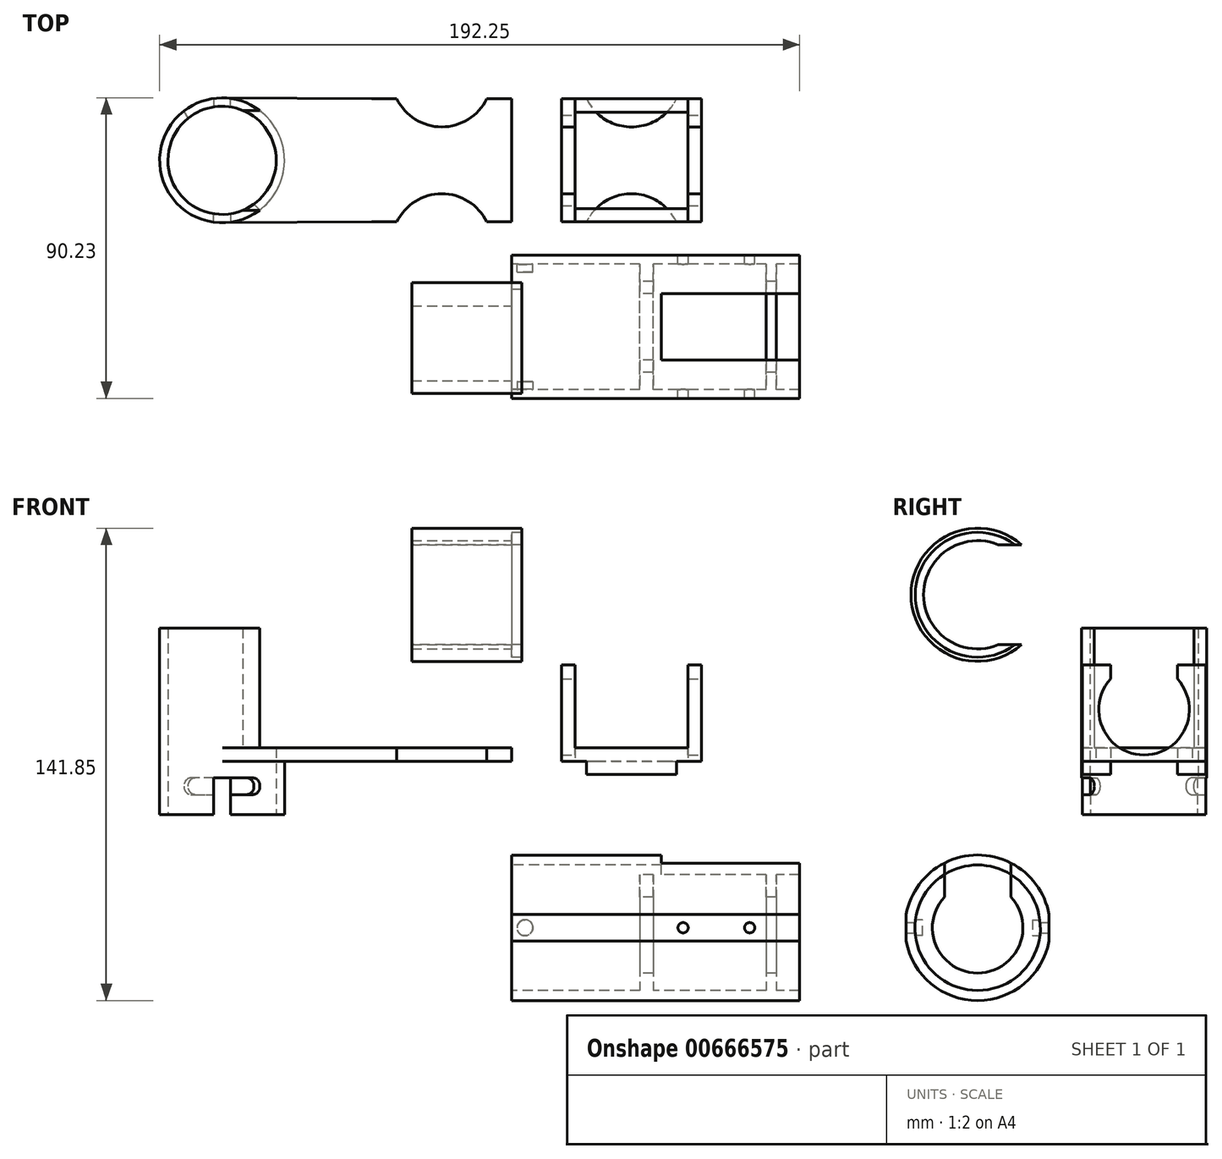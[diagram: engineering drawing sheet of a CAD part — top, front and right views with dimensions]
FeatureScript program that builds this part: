
annotation { "Feature Type Name" : "Feature", "Feature Type Description" : "" }
export const myFeature = defineFeature(function(context is Context, id is Id, definition is map)
    precondition{}
    {
        {
            var Q0;
            Q0=qCreatedBy(makeId("Top.planeOp"),FACE);
            var sketch = newSketch(context, id + "F0", { "sketchPlane" : qUnion([Q0])});
            skLineSegment(sketch, "E0.bottom", {"start": v(0, 18.5) * mm, "end": v(-42, 18.5) * mm});
            skLineSegment(sketch, "E0.top", {"start": v(0, -18.5) * mm, "end": v(-42, -18.5) * mm});
            skLineSegment(sketch, "E0.left", {"start": v(0, 18.5) * mm, "end": v(0, -18.5) * mm});
            skLineSegment(sketch, "E0.right", {"start": v(-42, 18.5) * mm, "end": v(-42, -18.5) * mm});
            skLineSegment(sketch, "E1.bottom", {"start": v(15, 18.5) * mm, "end": v(57, 18.5) * mm});
            skLineSegment(sketch, "E1.top", {"start": v(15, -18.5) * mm, "end": v(57, -18.5) * mm});
            skLineSegment(sketch, "E1.left", {"start": v(15, 18.5) * mm, "end": v(15, -18.5) * mm});
            skLineSegment(sketch, "E1.right", {"start": v(57, 18.5) * mm, "end": v(57, -18.5) * mm});
            skLineSegment(sketch, "E2", {"start": v(19, 18.5) * mm, "end": v(19, -18.5) * mm});
            skLineSegment(sketch, "E3", {"start": v(53, 18.5) * mm, "end": v(53, -18.5) * mm});
            skLineSegment(sketch, "E4", {"start": v(57, -14.5) * mm, "end": v(15, -14.5) * mm});
            skLineSegment(sketch, "E5", {"start": v(15, 14.5) * mm, "end": v(57, 14.5) * mm});
            skArc(sketch, "E6", {"start": v(22.5, 18.5) * mm, "mid": v(36, 10.04) * mm, "end": v(49.5, 18.5) * mm});
            skArc(sketch, "E7.MirrorCS", {"start": v(22.5, -18.5) * mm, "mid": v(36, -10.04) * mm, "end": v(49.5, -18.5) * mm});
            skCircle(sketch, "E8", {"center": v(-87, 0) * mm, "radius": 16.25 * mm});
            skPoint(sketch, "E8.centerSnap0", {"position": v(-42, 0) * mm});
            skCircle(sketch, "E9", {"center": v(-87, 0) * mm, "radius": 18.75 * mm});
            skLineSegment(sketch, "E10", {"start": v(-42, 18.5) * mm, "end": v(-86.9, 18.75) * mm});
            skLineSegment(sketch, "E11.MirrorCS", {"start": v(-42, -18.5) * mm, "end": v(-86.9, -18.75) * mm});
            skLineSegment(sketch, "E12", {"start": v(-80.75, 15) * mm, "end": v(-75.75, 15) * mm});
            skLineSegment(sketch, "E13.MirrorCS", {"start": v(-80.75, -15) * mm, "end": v(-75.75, -15) * mm});
            skArc(sketch, "E14", {"start": v(-7.5, -18.5) * mm, "mid": v(-21, -10.04) * mm, "end": v(-34.5, -18.5) * mm});
            skArc(sketch, "E15.MirrorCS", {"start": v(-7.5, 18.5) * mm, "mid": v(-21, 10.04) * mm, "end": v(-34.5, 18.5) * mm});
            skSolve(sketch);
        }
        {
            var Q0;
            {var subQ0=sQuery(id+"F0.wireOp",EDGE,"E0.left");Q0=makeQuery(id+"F0.imprint","IMPRINT",FACE,{"disambiguationData":[TD([[makeQuery(id+"F0.imprint","IMPRINT",EDGE,{"derivedFrom":subQ0}),-1.0]])]});}
            extrude(context, id + "F1", {"entities" : qUnion([Q0]), "depth" : 4 * mm, "offsetDistance" : 25 * mm});
        }
        {
            var Q0;
            {var subQ0=sQuery(id+"F0.wireOp",EDGE,"E4");var subQ1=sQuery(id+"F0.wireOp",EDGE,"E1.left");var subQ2=makeQuery(id+"F0.imprint","INTERSECT",VERTEX,{"derivedFrom":[subQ1,subQ0]});Q0=makeQuery(id+"F0.imprint","IMPRINT",FACE,{"disambiguationData":[TD([[makeQuery(id+"F0.imprint","IMPRINT",EDGE,{"disambiguationData":[TD([[subQ2,1.0]])],"derivedFrom":subQ1}),1.0]])]});}
            var Q1;
            {var subQ0=sQuery(id+"F0.wireOp",EDGE,"E1.left");var subQ1=sQuery(id+"F0.wireOp",EDGE,"E1.top");var subQ2=makeQuery(id+"F0.imprint","INTERSECT",VERTEX,{"derivedFrom":[subQ1,subQ0]});Q1=makeQuery(id+"F0.imprint","IMPRINT",FACE,{"disambiguationData":[TD([[makeQuery(id+"F0.imprint","IMPRINT",EDGE,{"disambiguationData":[TD([[subQ2,-1.0]])],"derivedFrom":subQ1}),1.0]])]});}
            var Q2;
            {var subQ0=sQuery(id+"F0.wireOp",EDGE,"E1.left");var subQ1=sQuery(id+"F0.wireOp",EDGE,"E1.bottom");var subQ2=makeQuery(id+"F0.imprint","INTERSECT",VERTEX,{"derivedFrom":[subQ1,subQ0]});Q2=makeQuery(id+"F0.imprint","IMPRINT",FACE,{"disambiguationData":[TD([[makeQuery(id+"F0.imprint","IMPRINT",EDGE,{"disambiguationData":[TD([[subQ2,-1.0]])],"derivedFrom":subQ1}),-1.0]])]});}
            var Q3;
            {var subQ0=sQuery(id+"F0.wireOp",EDGE,"E2");var subQ1=sQuery(id+"F0.wireOp",EDGE,"E1.bottom");var subQ2=makeQuery(id+"F0.imprint","INTERSECT",VERTEX,{"derivedFrom":[subQ1,subQ0]});Q3=makeQuery(id+"F0.imprint","IMPRINT",FACE,{"disambiguationData":[TD([[makeQuery(id+"F0.imprint","IMPRINT",EDGE,{"disambiguationData":[TD([[subQ2,-1.0]])],"derivedFrom":subQ1}),-1.0]])]});}
            var Q4;
            {var subQ0=sQuery(id+"F0.wireOp",EDGE,"E6");var subQ1=sQuery(id+"F0.wireOp",EDGE,"E1.bottom");var subQ2=makeQuery(id+"F0.imprint","INTERSECT",VERTEX,{"disambiguationData":[OD(0.0)],"derivedFrom":[subQ1,subQ0]});Q4=makeQuery(id+"F0.imprint","IMPRINT",FACE,{"disambiguationData":[TD([[makeQuery(id+"F0.imprint","IMPRINT",EDGE,{"disambiguationData":[TD([[subQ2,-1.0]])],"derivedFrom":subQ1}),-1.0]])]});}
            var Q5;
            {var subQ0=sQuery(id+"F0.wireOp",EDGE,"E3");var subQ1=sQuery(id+"F0.wireOp",EDGE,"E1.bottom");var subQ2=makeQuery(id+"F0.imprint","INTERSECT",VERTEX,{"derivedFrom":[subQ1,subQ0]});Q5=makeQuery(id+"F0.imprint","IMPRINT",FACE,{"disambiguationData":[TD([[makeQuery(id+"F0.imprint","IMPRINT",EDGE,{"disambiguationData":[TD([[subQ2,1.0]])],"derivedFrom":subQ1}),-1.0]])]});}
            var Q6;
            {var subQ0=sQuery(id+"F0.wireOp",EDGE,"E1.right");var subQ1=sQuery(id+"F0.wireOp",EDGE,"E1.bottom");var subQ2=makeQuery(id+"F0.imprint","INTERSECT",VERTEX,{"derivedFrom":[subQ1,subQ0]});Q6=makeQuery(id+"F0.imprint","IMPRINT",FACE,{"disambiguationData":[TD([[makeQuery(id+"F0.imprint","IMPRINT",EDGE,{"disambiguationData":[TD([[subQ2,1.0]])],"derivedFrom":subQ1}),-1.0]])]});}
            var Q7;
            {var subQ0=sQuery(id+"F0.wireOp",EDGE,"E4");var subQ1=sQuery(id+"F0.wireOp",EDGE,"E1.right");var subQ2=makeQuery(id+"F0.imprint","INTERSECT",VERTEX,{"derivedFrom":[subQ1,subQ0]});Q7=makeQuery(id+"F0.imprint","IMPRINT",FACE,{"disambiguationData":[TD([[makeQuery(id+"F0.imprint","IMPRINT",EDGE,{"disambiguationData":[TD([[subQ2,1.0]])],"derivedFrom":subQ1}),-1.0]])]});}
            var Q8;
            {var subQ0=sQuery(id+"F0.wireOp",EDGE,"E1.right");var subQ1=sQuery(id+"F0.wireOp",EDGE,"E1.top");var subQ2=makeQuery(id+"F0.imprint","INTERSECT",VERTEX,{"derivedFrom":[subQ1,subQ0]});Q8=makeQuery(id+"F0.imprint","IMPRINT",FACE,{"disambiguationData":[TD([[makeQuery(id+"F0.imprint","IMPRINT",EDGE,{"disambiguationData":[TD([[subQ2,1.0]])],"derivedFrom":subQ1}),1.0]])]});}
            var Q9;
            {var subQ0=sQuery(id+"F0.wireOp",EDGE,"E7.MirrorCS");var subQ1=sQuery(id+"F0.wireOp",EDGE,"E1.top");var subQ2=makeQuery(id+"F0.imprint","INTERSECT",VERTEX,{"disambiguationData":[OD(0.0)],"derivedFrom":[subQ1,subQ0]});Q9=makeQuery(id+"F0.imprint","IMPRINT",FACE,{"disambiguationData":[TD([[makeQuery(id+"F0.imprint","IMPRINT",EDGE,{"disambiguationData":[TD([[subQ2,-1.0]])],"derivedFrom":subQ1}),1.0]])]});}
            var Q10;
            {var subQ0=sQuery(id+"F0.wireOp",EDGE,"E3");var subQ1=sQuery(id+"F0.wireOp",EDGE,"E1.top");var subQ2=makeQuery(id+"F0.imprint","INTERSECT",VERTEX,{"derivedFrom":[subQ1,subQ0]});Q10=makeQuery(id+"F0.imprint","IMPRINT",FACE,{"disambiguationData":[TD([[makeQuery(id+"F0.imprint","IMPRINT",EDGE,{"disambiguationData":[TD([[subQ2,1.0]])],"derivedFrom":subQ1}),1.0]])]});}
            var Q11;
            {var subQ0=sQuery(id+"F0.wireOp",EDGE,"E2");var subQ1=sQuery(id+"F0.wireOp",EDGE,"E1.top");var subQ2=makeQuery(id+"F0.imprint","INTERSECT",VERTEX,{"derivedFrom":[subQ1,subQ0]});Q11=makeQuery(id+"F0.imprint","IMPRINT",FACE,{"disambiguationData":[TD([[makeQuery(id+"F0.imprint","IMPRINT",EDGE,{"disambiguationData":[TD([[subQ2,-1.0]])],"derivedFrom":subQ1}),1.0]])]});}
            extrude(context, id + "F2", {"entities" : qUnion([Q0, Q1, Q2, Q3, Q4, Q5, Q6, Q7, Q8, Q9, Q10, Q11]), "depth" : 4 * mm, "offsetDistance" : 25 * mm});
        }
        {
            var Q0;
            {var subQ0=sQuery(id+"F0.wireOp",EDGE,"E7.MirrorCS");var subQ1=sQuery(id+"F0.wireOp",EDGE,"E4");var subQ2=makeQuery(id+"F0.imprint","INTERSECT",VERTEX,{"disambiguationData":[OD(0.0)],"derivedFrom":[subQ1,subQ0]});Q0=makeQuery(id+"F0.imprint","IMPRINT",FACE,{"disambiguationData":[TD([[makeQuery(id+"F0.imprint","IMPRINT",EDGE,{"disambiguationData":[TD([[subQ2,-1.0]])],"derivedFrom":subQ1}),-1.0]])]});}
            var Q1;
            {var subQ0=sQuery(id+"F0.wireOp",EDGE,"E7.MirrorCS");var subQ1=sQuery(id+"F0.wireOp",EDGE,"E1.top");var subQ2=makeQuery(id+"F0.imprint","INTERSECT",VERTEX,{"disambiguationData":[OD(0.0)],"derivedFrom":[subQ1,subQ0]});Q1=makeQuery(id+"F0.imprint","IMPRINT",FACE,{"disambiguationData":[TD([[makeQuery(id+"F0.imprint","IMPRINT",EDGE,{"disambiguationData":[TD([[subQ2,-1.0]])],"derivedFrom":subQ1}),1.0]])]});}
            var Q2;
            {var subQ0=sQuery(id+"F0.wireOp",EDGE,"E6");var subQ1=sQuery(id+"F0.wireOp",EDGE,"E5");var subQ2=makeQuery(id+"F0.imprint","INTERSECT",VERTEX,{"disambiguationData":[OD(0.0)],"derivedFrom":[subQ1,subQ0]});Q2=makeQuery(id+"F0.imprint","IMPRINT",FACE,{"disambiguationData":[TD([[makeQuery(id+"F0.imprint","IMPRINT",EDGE,{"disambiguationData":[TD([[subQ2,-1.0]])],"derivedFrom":subQ1}),-1.0]])]});}
            var Q3;
            {var subQ0=sQuery(id+"F0.wireOp",EDGE,"E6");var subQ1=sQuery(id+"F0.wireOp",EDGE,"E1.bottom");var subQ2=makeQuery(id+"F0.imprint","INTERSECT",VERTEX,{"disambiguationData":[OD(0.0)],"derivedFrom":[subQ1,subQ0]});Q3=makeQuery(id+"F0.imprint","IMPRINT",FACE,{"disambiguationData":[TD([[makeQuery(id+"F0.imprint","IMPRINT",EDGE,{"disambiguationData":[TD([[subQ2,-1.0]])],"derivedFrom":subQ1}),-1.0]])]});}
            extrude(context, id + "F3", {"entities" : qUnion([Q0, Q1, Q2, Q3]), "operationType" : NewBodyOperationType.ADD, "oppositeDirection" : true, "depth" : 4 * mm, "offsetDistance" : 25 * mm});
        }
        {
            var Q0;
            {var subQ0=sQuery(id+"F0.wireOp",EDGE,"E1.left");var subQ1=sQuery(id+"F0.wireOp",EDGE,"E1.bottom");var subQ2=makeQuery(id+"F0.imprint","INTERSECT",VERTEX,{"derivedFrom":[subQ1,subQ0]});Q0=makeQuery(id+"F0.imprint","IMPRINT",FACE,{"disambiguationData":[TD([[makeQuery(id+"F0.imprint","IMPRINT",EDGE,{"disambiguationData":[TD([[subQ2,-1.0]])],"derivedFrom":subQ1}),-1.0]])]});}
            var Q1;
            {var subQ0=sQuery(id+"F0.wireOp",EDGE,"E1.left");var subQ1=sQuery(id+"F0.wireOp",EDGE,"E1.top");var subQ2=makeQuery(id+"F0.imprint","INTERSECT",VERTEX,{"derivedFrom":[subQ1,subQ0]});Q1=makeQuery(id+"F0.imprint","IMPRINT",FACE,{"disambiguationData":[TD([[makeQuery(id+"F0.imprint","IMPRINT",EDGE,{"disambiguationData":[TD([[subQ2,-1.0]])],"derivedFrom":subQ1}),1.0]])]});}
            var Q2;
            {var subQ0=sQuery(id+"F0.wireOp",EDGE,"E4");var subQ1=sQuery(id+"F0.wireOp",EDGE,"E1.left");var subQ2=makeQuery(id+"F0.imprint","INTERSECT",VERTEX,{"derivedFrom":[subQ1,subQ0]});Q2=makeQuery(id+"F0.imprint","IMPRINT",FACE,{"disambiguationData":[TD([[makeQuery(id+"F0.imprint","IMPRINT",EDGE,{"disambiguationData":[TD([[subQ2,1.0]])],"derivedFrom":subQ1}),1.0]])]});}
            var Q3;
            {var subQ0=sQuery(id+"F0.wireOp",EDGE,"E1.right");var subQ1=sQuery(id+"F0.wireOp",EDGE,"E1.bottom");var subQ2=makeQuery(id+"F0.imprint","INTERSECT",VERTEX,{"derivedFrom":[subQ1,subQ0]});Q3=makeQuery(id+"F0.imprint","IMPRINT",FACE,{"disambiguationData":[TD([[makeQuery(id+"F0.imprint","IMPRINT",EDGE,{"disambiguationData":[TD([[subQ2,1.0]])],"derivedFrom":subQ1}),-1.0]])]});}
            var Q4;
            {var subQ0=sQuery(id+"F0.wireOp",EDGE,"E4");var subQ1=sQuery(id+"F0.wireOp",EDGE,"E1.right");var subQ2=makeQuery(id+"F0.imprint","INTERSECT",VERTEX,{"derivedFrom":[subQ1,subQ0]});Q4=makeQuery(id+"F0.imprint","IMPRINT",FACE,{"disambiguationData":[TD([[makeQuery(id+"F0.imprint","IMPRINT",EDGE,{"disambiguationData":[TD([[subQ2,1.0]])],"derivedFrom":subQ1}),-1.0]])]});}
            var Q5;
            {var subQ0=sQuery(id+"F0.wireOp",EDGE,"E1.right");var subQ1=sQuery(id+"F0.wireOp",EDGE,"E1.top");var subQ2=makeQuery(id+"F0.imprint","INTERSECT",VERTEX,{"derivedFrom":[subQ1,subQ0]});Q5=makeQuery(id+"F0.imprint","IMPRINT",FACE,{"disambiguationData":[TD([[makeQuery(id+"F0.imprint","IMPRINT",EDGE,{"disambiguationData":[TD([[subQ2,1.0]])],"derivedFrom":subQ1}),1.0]])]});}
            extrude(context, id + "F4", {"entities" : qUnion([Q0, Q1, Q2, Q3, Q4, Q5]), "operationType" : NewBodyOperationType.ADD, "depth" : 34 * mm, "offsetDistance" : 25 * mm});
        }
        {
            var Q0;
            {var subQ0=sQuery(id+"F0.wireOp",EDGE,"E1.right");Q0=makeQuery(id+"F4.boolean.opBoolean","MERGE",FACE,{"derivedFrom":[makeQuery(id+"F2.opExtrude","SWEPT_FACE",FACE,{"disambiguationData":[OSD([subQ0])]}),makeQuery(id+"F4.opExtrude","SWEPT_FACE",FACE,{"disambiguationData":[OSD([subQ0])]})]});}
            var sketch = newSketch(context, id + "F5", { "sketchPlane" : qUnion([Q0])});
            skCircle(sketch, "E16", {"center": v(0, 15.5) * mm, "radius": 13.6 * mm});
            skPoint(sketch, "E16.centerSnap0", {"position": v(0, 34) * mm});
            skLineSegment(sketch, "E17", {"start": v(0, 34) * mm, "end": v(10, 34) * mm});
            skLineSegment(sketch, "E18", {"start": v(10, 34) * mm, "end": v(10, 24.72) * mm});
            skLineSegment(sketch, "E19.MirrorCS", {"start": v(0, 34) * mm, "end": v(-10, 34) * mm});
            skLineSegment(sketch, "E20.MirrorCS", {"start": v(-10, 34) * mm, "end": v(-10, 24.72) * mm});
            skSolve(sketch);
        }
        {
            var Q0;
            Q0 = qSketchRegion(id + "F5", true);
            extrude(context, id + "F6", {"entities" : qUnion([Q0]), "operationType" : NewBodyOperationType.REMOVE, "oppositeDirection" : true, "depth" : 50 * mm, "offsetDistance" : 25 * mm});
        }
        {
            var Q0;
            {var subQ0=sQuery(id+"F0.wireOp",EDGE,"E0.right");Q0=makeQuery(id+"F0.imprint","IMPRINT",FACE,{"disambiguationData":[TD([[makeQuery(id+"F0.imprint","IMPRINT",EDGE,{"derivedFrom":subQ0}),-1.0]])]});}
            var Q1;
            {var subQ0=sQuery(id+"F0.wireOp",EDGE,"E12");Q1=makeQuery(id+"F0.imprint","IMPRINT",FACE,{"disambiguationData":[TD([[makeQuery(id+"F0.imprint","IMPRINT",EDGE,{"derivedFrom":subQ0}),-1.0]])]});}
            extrude(context, id + "F7", {"entities" : qUnion([Q0, Q1]), "operationType" : NewBodyOperationType.ADD, "depth" : 4 * mm, "offsetDistance" : 25 * mm});
        }
        {
            var Q0;
            {var subQ3=sQuery(id+"F0.wireOp",EDGE,"E12");Q0=makeQuery(id+"F0.imprint","IMPRINT",FACE,{"disambiguationData":[TD([[makeQuery(id+"F0.imprint","IMPRINT",EDGE,{"derivedFrom":subQ3}),1.0]])]});}
            extrude(context, id + "F8", {"entities" : qUnion([Q0]), "operationType" : NewBodyOperationType.ADD, "depth" : 40 * mm, "offsetDistance" : 25 * mm});
        }
        {
            var Q0;
            {var subQ3=sQuery(id+"F0.wireOp",EDGE,"E12");Q0=makeQuery(id+"F0.imprint","IMPRINT",FACE,{"disambiguationData":[TD([[makeQuery(id+"F0.imprint","IMPRINT",EDGE,{"derivedFrom":subQ3}),1.0]])]});}
            var Q1;
            {var subQ0=sQuery(id+"F0.wireOp",EDGE,"E12");Q1=makeQuery(id+"F0.imprint","IMPRINT",FACE,{"disambiguationData":[TD([[makeQuery(id+"F0.imprint","IMPRINT",EDGE,{"derivedFrom":subQ0}),-1.0]])]});}
            var Q2;
            Q2 = qSketchRegion(id + "F10", true);
            extrude(context, id + "F9", {"entities" : qUnion([Q0, Q1, Q2]), "operationType" : NewBodyOperationType.ADD, "oppositeDirection" : true, "depth" : 20 * mm, "offsetDistance" : 25 * mm});
        }
        {
            var Q0;
            Q0=makeQuery(id+"F9.opExtrude","CAP_FACE",FACE,{"disambiguationData":[OSD([sQuery(id+"F0.wireOp",EDGE,"E8"),sQuery(id+"F0.wireOp",EDGE,"E9"),sQuery(id+"F0.wireOp",EDGE,"DEuqH4aA-ezls-Vg9X-zymG-u4QpP3lknrwe")])],"isStart":false});
            var sketch = newSketch(context, id + "F10", { "sketchPlane" : qUnion([Q0])});
            skLineSegment(sketch, "E21", {"start": v(-84.5, -16.06) * mm, "end": v(-84.5, -18.58) * mm});
            skLineSegment(sketch, "E22", {"start": v(-89.5, -18.58) * mm, "end": v(-89.5, -16.06) * mm});
            skLineSegment(sketch, "E23", {"start": v(-87, 0) * mm, "end": v(-87, 39.94) * mm, "construction": true});
            skLineSegment(sketch, "E24", {"start": v(-87, 0) * mm, "end": v(-108.18, 0) * mm, "construction": true});
            skLineSegment(sketch, "E25.MirrorCS", {"start": v(-89.5, 18.58) * mm, "end": v(-89.5, 16.06) * mm});
            skLineSegment(sketch, "E26.MirrorCS", {"start": v(-84.5, 16.06) * mm, "end": v(-84.5, 18.58) * mm});
            skSolve(sketch);
        }
        {
            var Q0;
            {var subQ2=sQuery(id+"F10.wireOp",EDGE,"E21");Q0=makeQuery(id+"F10.imprint","IMPRINT",FACE,{"disambiguationData":[TD([[makeQuery(id+"F10.imprint","IMPRINT",EDGE,{"derivedFrom":subQ2}),-1.0]])]});}
            var Q1;
            {var subQ0=sQuery(id+"F10.wireOp",EDGE,"E25.MirrorCS");Q1=makeQuery(id+"F10.imprint","IMPRINT",FACE,{"disambiguationData":[TD([[makeQuery(id+"F10.imprint","IMPRINT",EDGE,{"derivedFrom":subQ0}),1.0]])]});}
            extrude(context, id + "F11", {"entities" : qUnion([Q0, Q1]), "operationType" : NewBodyOperationType.REMOVE, "oppositeDirection" : true, "depth" : 15 * mm, "offsetDistance" : 25 * mm});
        }
        {
            var Q0;
            Q0=makeQuery(id+"F11.boolean.opBoolean","COPY",FACE,{"derivedFrom":makeQuery(id+"F11.opExtrude","SWEPT_FACE",FACE,{"disambiguationData":[OSD([sQuery(id+"F10.wireOp",EDGE,"E25.MirrorCS")])]})});
            var sketch = newSketch(context, id + "F12", { "sketchPlane" : qUnion([Q0])});
            skLineSegment(sketch, "E27.bottom", {"start": v(-18.58, -5) * mm, "end": v(-16.06, -5) * mm});
            skLineSegment(sketch, "E27.top", {"start": v(-18.58, -10) * mm, "end": v(-16.06, -10) * mm});
            skLineSegment(sketch, "E27.left", {"start": v(-18.58, -5) * mm, "end": v(-18.58, -10) * mm});
            skLineSegment(sketch, "E27.right", {"start": v(-16.06, -5) * mm, "end": v(-16.06, -10) * mm});
            skSolve(sketch);
        }
        {
            var Q0;
            Q0=makeQuery(id+"F11.boolean.opBoolean","COPY",FACE,{"derivedFrom":makeQuery(id+"F11.opExtrude","SWEPT_FACE",FACE,{"disambiguationData":[OSD([sQuery(id+"F10.wireOp",EDGE,"E22")])]})});
            var sketch = newSketch(context, id + "F13", { "sketchPlane" : qUnion([Q0])});
            skLineSegment(sketch, "E28.bottom", {"start": v(16.06, -5) * mm, "end": v(18.58, -5) * mm});
            skLineSegment(sketch, "E28.top", {"start": v(16.06, -10) * mm, "end": v(18.58, -10) * mm});
            skLineSegment(sketch, "E28.left", {"start": v(16.06, -5) * mm, "end": v(16.06, -10) * mm});
            skLineSegment(sketch, "E28.right", {"start": v(18.58, -5) * mm, "end": v(18.58, -10) * mm});
            skSolve(sketch);
        }
        {
            var Q0;
            Q0=makeQuery(id+"F12.imprint","IMPRINT",FACE,{"disambiguationData":[TD([[makeQuery(id+"F12.imprint","IMPRINT",EDGE,{"derivedFrom":sQuery(id+"F12.wireOp",EDGE,"E27.bottom")}),-1.0]])]});
            var Q1;
            {var subQ0=sQuery(id+"F0.wireOp",EDGE,"DEuqH4aA-ezls-Vg9X-zymG-u4QpP3lknrwe");var subQ1=sQuery(id+"F0.wireOp",EDGE,"E9");var subQ2=sQuery(id+"F0.wireOp",EDGE,"E8");var subQ3=makeQuery(id+"F0.imprint","INTERSECT",VERTEX,{"derivedFrom":[subQ1,sQuery(id+"F0.wireOp",EDGE,"E11.MirrorCS")]});Q1=makeQuery(id+"FEjkLrXl29dIm0a_0.boolean.opBoolean","SPLIT",FACE,{"disambiguationData":[TD([makeQuery(id+"F9.opExtrude","CAP_FACE",FACE,{"disambiguationData":[OSD([subQ2,subQ1,subQ0])],"isStart":false})])],"derivedFrom":makeQuery(id+"F9.boolean.opBoolean","MERGE",FACE,{"derivedFrom":[makeQuery(id+"F8.opExtrude","SWEPT_FACE",FACE,{"disambiguationData":[OSD([subQ1]),TDD([makeQuery(id+"F0.imprint","IMPRINT",EDGE,{"disambiguationData":[TD([[makeQuery(id+"F0.imprint","INTERSECT",VERTEX,{"disambiguationData":[OD(0.0)],"derivedFrom":[subQ1,subQ0]}),-1.0]])],"derivedFrom":subQ1}),makeQuery(id+"F0.imprint","IMPRINT",EDGE,{"disambiguationData":[TD([[subQ3,-1.0]])],"derivedFrom":subQ1})])]}),makeQuery(id+"F9.opExtrude","SWEPT_FACE",FACE,{"disambiguationData":[OSD([subQ1])]})]})});}
            revolve(context, id + "F14", {"operationType" : NewBodyOperationType.REMOVE, "entities" : qUnion([Q0]), "axis" : qUnion([Q1]), "revolveType" : RevolveType.ONE_DIRECTION, "oppositeDirection" : true, "angle" : 45 * degree});
        }
        {
            var Q0;
            Q0=makeQuery(id+"F13.imprint","IMPRINT",FACE,{"disambiguationData":[TD([[makeQuery(id+"F13.imprint","IMPRINT",EDGE,{"derivedFrom":sQuery(id+"F13.wireOp",EDGE,"E28.bottom")}),1.0]])]});
            var Q1;
            {var subQ0=sQuery(id+"F0.wireOp",EDGE,"DEuqH4aA-ezls-Vg9X-zymG-u4QpP3lknrwe");var subQ1=sQuery(id+"F0.wireOp",EDGE,"E9");var subQ2=sQuery(id+"F0.wireOp",EDGE,"E8");Q1=makeQuery(id+"FEjkLrXl29dIm0a_0.boolean.opBoolean","SPLIT",FACE,{"disambiguationData":[TD([makeQuery(id+"F9.opExtrude","CAP_FACE",FACE,{"disambiguationData":[OSD([subQ2,subQ1,subQ0])],"isStart":false})])],"derivedFrom":makeQuery(id+"F9.boolean.opBoolean","MERGE",FACE,{"derivedFrom":[makeQuery(id+"F8.boolean.opBoolean","MERGE",FACE,{"derivedFrom":[makeQuery(id+"F7.opExtrude","SWEPT_FACE",FACE,{"disambiguationData":[OSD([subQ2])]}),makeQuery(id+"F8.opExtrude","SWEPT_FACE",FACE,{"disambiguationData":[OSD([subQ2])]})]}),makeQuery(id+"F9.opExtrude","SWEPT_FACE",FACE,{"disambiguationData":[OSD([subQ2])]})]})});}
            revolve(context, id + "F15", {"operationType" : NewBodyOperationType.REMOVE, "entities" : qUnion([Q0]), "axis" : qUnion([Q1]), "revolveType" : RevolveType.ONE_DIRECTION, "angle" : 30 * degree});
        }
        {
            var Q0;
            Q0=makeQuery(id+"F14.boolean.opBoolean","COPY",EDGE,{"derivedFrom":makeQuery(id+"F14.opRevolve","CAP_EDGE",EDGE,{"disambiguationData":[OSD([sQuery(id+"F12.wireOp",EDGE,"E27.bottom")]),OD(1.0)],"isStart":false})});
            var Q1;
            Q1=makeQuery(id+"F14.boolean.opBoolean","COPY",EDGE,{"derivedFrom":makeQuery(id+"F14.opRevolve","CAP_EDGE",EDGE,{"disambiguationData":[OSD([sQuery(id+"F12.wireOp",EDGE,"E27.top")]),OD(1.0)],"isStart":false})});
            var Q2;
            Q2=makeQuery(id+"F15.boolean.opBoolean","COPY",EDGE,{"derivedFrom":makeQuery(id+"F15.opRevolve","CAP_EDGE",EDGE,{"disambiguationData":[OSD([sQuery(id+"F13.wireOp",EDGE,"E28.top")]),OD(1.0)],"isStart":false})});
            var Q3;
            Q3=makeQuery(id+"F15.boolean.opBoolean","COPY",EDGE,{"derivedFrom":makeQuery(id+"F15.opRevolve","CAP_EDGE",EDGE,{"disambiguationData":[OSD([sQuery(id+"F13.wireOp",EDGE,"E28.bottom")]),OD(1.0)],"isStart":false})});
            fillet(context, id + "F16", {"entities" : qUnion([Q0, Q1, Q2, Q3]), "radius" : 2.5 * mm, "tangentPropagation" : true, "allowEdgeOverflow" : false});
        }
        {
            var Q0;
            Q0=makeQuery(id+"F5.imprint","IMPRINT",FACE,{"disambiguationData":[TD([[makeQuery(id+"F5.imprint","IMPRINT",EDGE,{"derivedFrom":sQuery(id+"F5.wireOp",EDGE,"E17")}),1.0]])]});
            extrude(context, id + "F17", {"entities" : qUnion([Q0]), "operationType" : NewBodyOperationType.REMOVE, "oppositeDirection" : true, "depth" : 55 * mm, "offsetDistance" : 25 * mm});
        }
        {
            var Q0;
            {var subQ0=sQuery(id+"F0.wireOp",EDGE,"E2");var subQ1=sQuery(id+"F0.wireOp",EDGE,"E1.top");var subQ2=sQuery(id+"F0.wireOp",EDGE,"E1.left");Q0=makeQuery(id+"F6.boolean.opBoolean","SPLIT",FACE,{"disambiguationData":[TD([makeQuery(id+"F2.opExtrude","SWEPT_FACE",FACE,{"disambiguationData":[OSD([subQ1])]})])],"derivedFrom":makeQuery(id+"F4.opExtrude","CAP_FACE",FACE,{"disambiguationData":[OSD([sQuery(id+"F0.wireOp",EDGE,"E1.bottom"),subQ1,subQ2,subQ0])],"isStart":false})});}
            var Q1;
            {var subQ0=sQuery(id+"F0.wireOp",EDGE,"E1.bottom");var subQ1=sQuery(id+"F0.wireOp",EDGE,"E1.right");var subQ2=sQuery(id+"F0.wireOp",EDGE,"E3");Q1=makeQuery(id+"F6.boolean.opBoolean","SPLIT",FACE,{"disambiguationData":[TD([makeQuery(id+"F2.opExtrude","SWEPT_FACE",FACE,{"disambiguationData":[OSD([subQ0])]})])],"derivedFrom":makeQuery(id+"F4.opExtrude","CAP_FACE",FACE,{"disambiguationData":[OSD([subQ0,sQuery(id+"F0.wireOp",EDGE,"E1.top"),subQ1,subQ2])],"isStart":false})});}
            var Q2;
            {var subQ0=sQuery(id+"F0.wireOp",EDGE,"E1.bottom");var subQ1=sQuery(id+"F0.wireOp",EDGE,"E1.left");var subQ2=sQuery(id+"F0.wireOp",EDGE,"E2");Q2=makeQuery(id+"F6.boolean.opBoolean","SPLIT",FACE,{"disambiguationData":[TD([makeQuery(id+"F2.opExtrude","SWEPT_FACE",FACE,{"disambiguationData":[OSD([subQ0])]})])],"derivedFrom":makeQuery(id+"F4.opExtrude","CAP_FACE",FACE,{"disambiguationData":[OSD([subQ0,sQuery(id+"F0.wireOp",EDGE,"E1.top"),subQ1,subQ2])],"isStart":false})});}
            var Q3;
            {var subQ0=sQuery(id+"F0.wireOp",EDGE,"E1.top");var subQ1=sQuery(id+"F0.wireOp",EDGE,"E3");var subQ2=sQuery(id+"F0.wireOp",EDGE,"E1.right");Q3=makeQuery(id+"F6.boolean.opBoolean","SPLIT",FACE,{"disambiguationData":[TD([makeQuery(id+"F2.opExtrude","SWEPT_FACE",FACE,{"disambiguationData":[OSD([subQ0])]})])],"derivedFrom":makeQuery(id+"F4.opExtrude","CAP_FACE",FACE,{"disambiguationData":[OSD([sQuery(id+"F0.wireOp",EDGE,"E1.bottom"),subQ0,subQ2,subQ1])],"isStart":false})});}
            extrude(context, id + "F18", {"entities" : qUnion([Q0, Q1, Q2, Q3]), "operationType" : NewBodyOperationType.REMOVE, "oppositeDirection" : true, "depth" : 5 * mm, "offsetDistance" : 25 * mm});
        }
        {
            var Q0;
            Q0=qCreatedBy(makeId("Right.planeOp"),FACE);
            var sketch = newSketch(context, id + "F19", { "sketchPlane" : qUnion([Q0])});
            skLineSegment(sketch, "E29", {"start": v(-50, 0) * mm, "end": v(-50, -109.68) * mm, "construction": true});
            skLineSegment(sketch, "E30", {"start": v(-90.75, -50) * mm, "end": v(-0.23, -50) * mm, "construction": true});
            skCircle(sketch, "E31", {"center": v(-50, -50) * mm, "radius": 18.85 * mm});
            skCircle(sketch, "E32", {"center": v(-50, -50) * mm, "radius": 21.85 * mm});
            skLineSegment(sketch, "E33", {"start": v(-60, -34.02) * mm, "end": v(-60, -30.57) * mm});
            skLineSegment(sketch, "E34.MirrorCS", {"start": v(-40, -34.02) * mm, "end": v(-40, -30.57) * mm});
            skLineSegment(sketch, "E35", {"start": v(-71.48, -54) * mm, "end": v(-71.48, -46) * mm});
            skLineSegment(sketch, "E36.MirrorCS", {"start": v(-28.52, -54) * mm, "end": v(-28.52, -46) * mm});
            skSolve(sketch);
        }
        {
            var Q0;
            {var subQ0=sQuery(id+"F19.wireOp",EDGE,"E33");Q0=makeQuery(id+"F19.imprint","IMPRINT",FACE,{"disambiguationData":[TD([[makeQuery(id+"F19.imprint","IMPRINT",EDGE,{"derivedFrom":subQ0}),1.0]])]});}
            extrude(context, id + "F20", {"entities" : qUnion([Q0]), "depth" : 38.5 * mm, "offsetDistance" : 25 * mm});
        }
        {
            var Q0;
            Q0=makeQuery(id+"F20.opExtrude","SWEPT_FACE",FACE,{"disambiguationData":[OSD([sQuery(id+"F19.wireOp",EDGE,"E35")])]});
            var sketch = newSketch(context, id + "F21", { "sketchPlane" : qUnion([Q0])});
            skLineSegment(sketch, "E37", {"start": v(0, -50) * mm, "end": v(38.5, -50) * mm, "construction": true});
            skCircle(sketch, "E38", {"center": v(4, -50) * mm, "radius": 2.4 * mm});
            skSolve(sketch);
        }
        {
            var Q0;
            Q0=makeQuery(id+"F20.opExtrude","SWEPT_FACE",FACE,{"disambiguationData":[OSD([sQuery(id+"F19.wireOp",EDGE,"E36.MirrorCS")])]});
            var sketch = newSketch(context, id + "F22", { "sketchPlane" : qUnion([Q0])});
            skLineSegment(sketch, "E39", {"start": v(0, -50) * mm, "end": v(-38.5, -50) * mm, "construction": true});
            skCircle(sketch, "E40", {"center": v(-4, -50) * mm, "radius": 2.4 * mm});
            skSolve(sketch);
        }
        {
            var Q0;
            Q0=makeQuery(id+"F21.imprint","IMPRINT",FACE,{"disambiguationData":[TD([[makeQuery(id+"F21.imprint","IMPRINT",EDGE,{"derivedFrom":sQuery(id+"F21.wireOp",EDGE,"E38")}),1.0]])]});
            extrude(context, id + "F23", {"entities" : qUnion([Q0]), "operationType" : NewBodyOperationType.ADD, "oppositeDirection" : true, "depth" : 5 * mm, "offsetDistance" : 25 * mm});
        }
        {
            var Q0;
            Q0=makeQuery(id+"F22.imprint","IMPRINT",FACE,{"disambiguationData":[TD([[makeQuery(id+"F22.imprint","IMPRINT",EDGE,{"derivedFrom":sQuery(id+"F22.wireOp",EDGE,"E40")}),1.0]])]});
            extrude(context, id + "F24", {"entities" : qUnion([Q0]), "operationType" : NewBodyOperationType.ADD, "oppositeDirection" : true, "depth" : 5 * mm, "offsetDistance" : 25 * mm});
        }
        {
            var Q0;
            {var subQ0=sQuery(id+"F19.wireOp",EDGE,"E33");Q0=makeQuery(id+"F19.imprint","IMPRINT",FACE,{"disambiguationData":[TD([[makeQuery(id+"F19.imprint","IMPRINT",EDGE,{"derivedFrom":subQ0}),-1.0]])]});}
            extrude(context, id + "F25", {"entities" : qUnion([Q0]), "operationType" : NewBodyOperationType.ADD, "depth" : 38.5 * mm, "offsetDistance" : 25 * mm});
        }
        {
            var Q0;
            {var subQ0=sQuery(id+"F0.wireOp",EDGE,"E8");var subQ1=sQuery(id+"F0.wireOp",EDGE,"E9");var subQ3=sQuery(id+"F0.wireOp",EDGE,"DEuqH4aA-ezls-Vg9X-zymG-u4QpP3lknrwe");Q0=makeQuery(id+"F11.boolean.opBoolean","SPLIT",FACE,{"disambiguationData":[TD([makeQuery(id+"F11.opExtrude","SWEPT_FACE",FACE,{"disambiguationData":[OSD([sQuery(id+"F10.wireOp",EDGE,"E22")])]})])],"derivedFrom":makeQuery(id+"F9.opExtrude","CAP_FACE",FACE,{"disambiguationData":[OSD([subQ0,subQ1,subQ3])],"isStart":false})});}
            var Q1;
            {var subQ0=sQuery(id+"F0.wireOp",EDGE,"E8");var subQ1=sQuery(id+"F0.wireOp",EDGE,"E9");var subQ3=sQuery(id+"F0.wireOp",EDGE,"DEuqH4aA-ezls-Vg9X-zymG-u4QpP3lknrwe");Q1=makeQuery(id+"F11.boolean.opBoolean","SPLIT",FACE,{"disambiguationData":[TD([makeQuery(id+"F11.opExtrude","SWEPT_FACE",FACE,{"disambiguationData":[OSD([sQuery(id+"F10.wireOp",EDGE,"E21")])]})])],"derivedFrom":makeQuery(id+"F9.opExtrude","CAP_FACE",FACE,{"disambiguationData":[OSD([subQ0,subQ1,subQ3])],"isStart":false})});}
            extrude(context, id + "F26", {"entities" : qUnion([Q0, Q1]), "operationType" : NewBodyOperationType.REMOVE, "oppositeDirection" : true, "depth" : 4 * mm, "offsetDistance" : 25 * mm});
        }
        {
            var Q0;
            {var subQ0=sQuery(id+"F19.wireOp",EDGE,"E34.MirrorCS");var subQ1=sQuery(id+"F19.wireOp",EDGE,"E33");var subQ2=sQuery(id+"F19.wireOp",EDGE,"E32");var subQ3=sQuery(id+"F19.wireOp",EDGE,"E31");Q0=makeQuery(id+"F25.boolean.opBoolean","MERGE",FACE,{"derivedFrom":[makeQuery(id+"F20.opExtrude","CAP_FACE",FACE,{"disambiguationData":[OSD([subQ3,subQ2,subQ1,subQ0,sQuery(id+"F19.wireOp",EDGE,"E35"),sQuery(id+"F19.wireOp",EDGE,"E36.MirrorCS")])],"isStart":false}),makeQuery(id+"F25.opExtrude","CAP_FACE",FACE,{"disambiguationData":[OSD([subQ3,subQ2,subQ1,subQ0])],"isStart":false})]});}
            var sketch = newSketch(context, id + "F27", { "sketchPlane" : qUnion([Q0])});
            skCircle(sketch, "E41", {"center": v(-50, -50) * mm, "radius": 13.6 * mm});
            skSolve(sketch);
        }
        {
            var Q0;
            Q0=makeQuery(id+"F27.imprint","IMPRINT",FACE,{"disambiguationData":[TD([[makeQuery(id+"F27.imprint","IMPRINT",EDGE,{"derivedFrom":sQuery(id+"F27.wireOp",EDGE,"E41")}),-1.0]])]});
            var Q1;
            {var subQ2=sQuery(id+"F19.wireOp",EDGE,"E35");Q1=makeQuery(id+"F27.imprint","IMPRINT",FACE,{"disambiguationData":[TD([[makeQuery(id+"F27.imprint","IMPRINT",EDGE,{"derivedFrom":makeQuery(id+"F20.opExtrude","CAP_EDGE",EDGE,{"disambiguationData":[OSD([subQ2])],"isStart":false})}),-1.0]])]});}
            extrude(context, id + "F28", {"entities" : qUnion([Q0, Q1]), "operationType" : NewBodyOperationType.ADD, "depth" : 4 * mm, "offsetDistance" : 25 * mm});
        }
        {
            var Q0;
            Q0=makeQuery(id+"F28.opExtrude","CAP_FACE",FACE,{"disambiguationData":[OSD([sQuery(id+"F19.wireOp",EDGE,"E32"),sQuery(id+"F19.wireOp",EDGE,"E35"),sQuery(id+"F19.wireOp",EDGE,"E36.MirrorCS"),sQuery(id+"F27.wireOp",EDGE,"E41")])],"isStart":false});
            var sketch = newSketch(context, id + "F29", { "sketchPlane" : qUnion([Q0])});
            skCircle(sketch, "E42", {"center": v(-50, -50) * mm, "radius": 18.85 * mm});
            skCircle(sketch, "E43", {"center": v(-50, -50) * mm, "radius": 21.85 * mm});
            skLineSegment(sketch, "E44", {"start": v(-50, -50) * mm, "end": v(-50, -22.72) * mm, "construction": true});
            skLineSegment(sketch, "E45", {"start": v(-40, -34.02) * mm, "end": v(-40, -40.78) * mm});
            skLineSegment(sketch, "E46.MirrorCS", {"start": v(-60, -34.02) * mm, "end": v(-60, -40.78) * mm});
            skSolve(sketch);
        }
        {
            var Q0;
            Q0=makeQuery(id+"F29.imprint","IMPRINT",FACE,{"disambiguationData":[TD([[makeQuery(id+"F29.imprint","IMPRINT",EDGE,{"derivedFrom":sQuery(id+"F29.wireOp",EDGE,"E42")}),-1.0]])]});
            extrude(context, id + "F30", {"entities" : qUnion([Q0]), "operationType" : NewBodyOperationType.ADD, "depth" : 34 * mm, "offsetDistance" : 25 * mm});
        }
        {
            var Q0;
            Q0=makeQuery(id+"F30.opExtrude","CAP_FACE",FACE,{"disambiguationData":[OSD([sQuery(id+"F19.wireOp",EDGE,"E35"),sQuery(id+"F19.wireOp",EDGE,"E36.MirrorCS"),sQuery(id+"F29.wireOp",EDGE,"E42"),sQuery(id+"F29.wireOp",EDGE,"E43")])],"isStart":false});
            var sketch = newSketch(context, id + "F31", { "sketchPlane" : qUnion([Q0])});
            skCircle(sketch, "E47", {"center": v(-50, -50) * mm, "radius": 13.6 * mm});
            skCircle(sketch, "E48", {"center": v(-50, -50) * mm, "radius": 18.85 * mm});
            skCircle(sketch, "E49", {"center": v(-50, -50) * mm, "radius": 21.85 * mm});
            skSolve(sketch);
        }
        {
            var Q0;
            Q0=makeQuery(id+"F30.opExtrude","CAP_FACE",FACE,{"disambiguationData":[OSD([sQuery(id+"F19.wireOp",EDGE,"E35"),sQuery(id+"F19.wireOp",EDGE,"E36.MirrorCS"),sQuery(id+"F29.wireOp",EDGE,"E42"),sQuery(id+"F29.wireOp",EDGE,"E43")])],"isStart":false});
            extrude(context, id + "F32", {"entities" : qUnion([Q0]), "operationType" : NewBodyOperationType.ADD, "depth" : 10 * mm, "offsetDistance" : 25 * mm});
        }
        {
            var Q0;
            Q0=makeQuery(id+"F31.imprint","IMPRINT",FACE,{"disambiguationData":[TD([[makeQuery(id+"F31.imprint","IMPRINT",EDGE,{"derivedFrom":sQuery(id+"F31.wireOp",EDGE,"E47")}),-1.0]])]});
            extrude(context, id + "F33", {"entities" : qUnion([Q0]), "operationType" : NewBodyOperationType.ADD, "depth" : 3 * mm, "offsetDistance" : 25 * mm});
        }
        {
            var Q0;
            {var subQ0=sQuery(id+"F19.wireOp",EDGE,"E33");Q0=makeQuery(id+"F19.imprint","IMPRINT",FACE,{"disambiguationData":[TD([[makeQuery(id+"F19.imprint","IMPRINT",EDGE,{"derivedFrom":subQ0}),-1.0]])]});}
            extrude(context, id + "F34", {"entities" : qUnion([Q0]), "operationType" : NewBodyOperationType.REMOVE, "depth" : 90 * mm, "offsetDistance" : 25 * mm});
        }
        {
            var Q0;
            {var subQ0=sQuery(id+"F29.wireOp",EDGE,"E45");Q0=makeQuery(id+"F29.imprint","IMPRINT",FACE,{"disambiguationData":[TD([[makeQuery(id+"F29.imprint","IMPRINT",EDGE,{"derivedFrom":subQ0}),-1.0]])]});}
            extrude(context, id + "F35", {"entities" : qUnion([Q0]), "operationType" : NewBodyOperationType.REMOVE, "depth" : 40 * mm, "offsetDistance" : 25 * mm, "hasSecondDirection" : true, "secondDirectionOppositeDirection" : true, "secondDirectionDepth" : 5 * mm});
        }
        {
            var Q0;
            {var subQ0=sQuery(id+"F19.wireOp",EDGE,"E33");Q0=makeQuery(id+"F19.imprint","IMPRINT",FACE,{"disambiguationData":[TD([[makeQuery(id+"F19.imprint","IMPRINT",EDGE,{"derivedFrom":subQ0}),-1.0]])]});}
            extrude(context, id + "F36", {"entities" : qUnion([Q0]), "operationType" : NewBodyOperationType.ADD, "depth" : 45 * mm, "offsetDistance" : 25 * mm});
        }
        {
            var Q0;
            {var subQ0=sQuery(id+"F19.wireOp",EDGE,"E36.MirrorCS");Q0=makeQuery(id+"F32.boolean.opBoolean","MERGE",FACE,{"derivedFrom":[makeQuery(id+"F30.boolean.opBoolean","MERGE",FACE,{"derivedFrom":[makeQuery(id+"F28.boolean.opBoolean","MERGE",FACE,{"derivedFrom":[makeQuery(id+"F20.opExtrude","SWEPT_FACE",FACE,{"disambiguationData":[OSD([subQ0])]}),makeQuery(id+"F28.opExtrude","SWEPT_FACE",FACE,{"disambiguationData":[OSD([subQ0])]})]}),makeQuery(id+"F30.opExtrude","SWEPT_FACE",FACE,{"disambiguationData":[OSD([subQ0])]})]}),makeQuery(id+"F32.opExtrude","SWEPT_FACE",FACE,{"disambiguationData":[OSD([subQ0])]})]});}
            var sketch = newSketch(context, id + "F37", { "sketchPlane" : qUnion([Q0])});
            skLineSegment(sketch, "E50", {"start": v(-86.5, -50) * mm, "end": v(0, -50) * mm, "construction": true});
            skCircle(sketch, "E51", {"center": v(-71.5, -50) * mm, "radius": 1.55 * mm});
            skCircle(sketch, "E52", {"center": v(-51.5, -50) * mm, "radius": 1.55 * mm});
            skSolve(sketch);
        }
        {
            var Q0;
            Q0=makeQuery(id+"F37.imprint","IMPRINT",FACE,{"disambiguationData":[TD([[makeQuery(id+"F37.imprint","IMPRINT",EDGE,{"derivedFrom":sQuery(id+"F37.wireOp",EDGE,"E51")}),1.0]])]});
            var Q1;
            Q1=makeQuery(id+"F37.imprint","IMPRINT",FACE,{"disambiguationData":[TD([[makeQuery(id+"F37.imprint","IMPRINT",EDGE,{"derivedFrom":sQuery(id+"F37.wireOp",EDGE,"E52")}),1.0]])]});
            extrude(context, id + "F38", {"entities" : qUnion([Q0, Q1]), "operationType" : NewBodyOperationType.REMOVE, "oppositeDirection" : true, "depth" : 60 * mm, "offsetDistance" : 25 * mm});
        }
        {
            var Q0;
            Q0=qCreatedBy(makeId("Right.planeOp"),FACE);
            var sketch = newSketch(context, id + "F39", { "sketchPlane" : qUnion([Q0])});
            skLineSegment(sketch, "E53", {"start": v(0, 50) * mm, "end": v(-100.67, 50) * mm, "construction": true});
            skLineSegment(sketch, "E54", {"start": v(-50, 18.03) * mm, "end": v(-50, 118.7) * mm, "construction": true});
            skCircle(sketch, "E55", {"center": v(-50, 50) * mm, "radius": 18.75 * mm});
            skCircle(sketch, "E56", {"center": v(-50, 50) * mm, "radius": 16.25 * mm});
            skLineSegment(sketch, "E57", {"start": v(-43.75, 65) * mm, "end": v(-38.75, 65) * mm});
            skLineSegment(sketch, "E58.MirrorCS", {"start": v(-43.75, 35) * mm, "end": v(-38.75, 35) * mm});
            skCircle(sketch, "E59", {"center": v(-50, 50) * mm, "radius": 20 * mm});
            skLineSegment(sketch, "E60", {"start": v(-38.75, 65) * mm, "end": v(-36.77, 65) * mm});
            skLineSegment(sketch, "E61.MirrorCS", {"start": v(-38.75, 35) * mm, "end": v(-36.77, 35) * mm});
            skSolve(sketch);
        }
        {
            var Q0;
            {var subQ0=sQuery(id+"F39.wireOp",EDGE,"E60");Q0=makeQuery(id+"F39.imprint","IMPRINT",FACE,{"disambiguationData":[TD([[makeQuery(id+"F39.imprint","IMPRINT",EDGE,{"derivedFrom":subQ0}),1.0]])]});}
            extrude(context, id + "F40", {"entities" : qUnion([Q0]), "depth" : 3 * mm, "offsetDistance" : 25 * mm});
        }
        {
            var Q0;
            {var subQ0=sQuery(id+"F39.wireOp",EDGE,"E57");Q0=makeQuery(id+"F39.imprint","IMPRINT",FACE,{"disambiguationData":[TD([[makeQuery(id+"F39.imprint","IMPRINT",EDGE,{"derivedFrom":subQ0}),1.0]])]});}
            var Q1;
            {var subQ0=sQuery(id+"F39.wireOp",EDGE,"E60");Q1=makeQuery(id+"F39.imprint","IMPRINT",FACE,{"disambiguationData":[TD([[makeQuery(id+"F39.imprint","IMPRINT",EDGE,{"derivedFrom":subQ0}),1.0]])]});}
            extrude(context, id + "F41", {"entities" : qUnion([Q0, Q1]), "operationType" : NewBodyOperationType.ADD, "oppositeDirection" : true, "depth" : 30 * mm, "offsetDistance" : 25 * mm});
        }
    });
